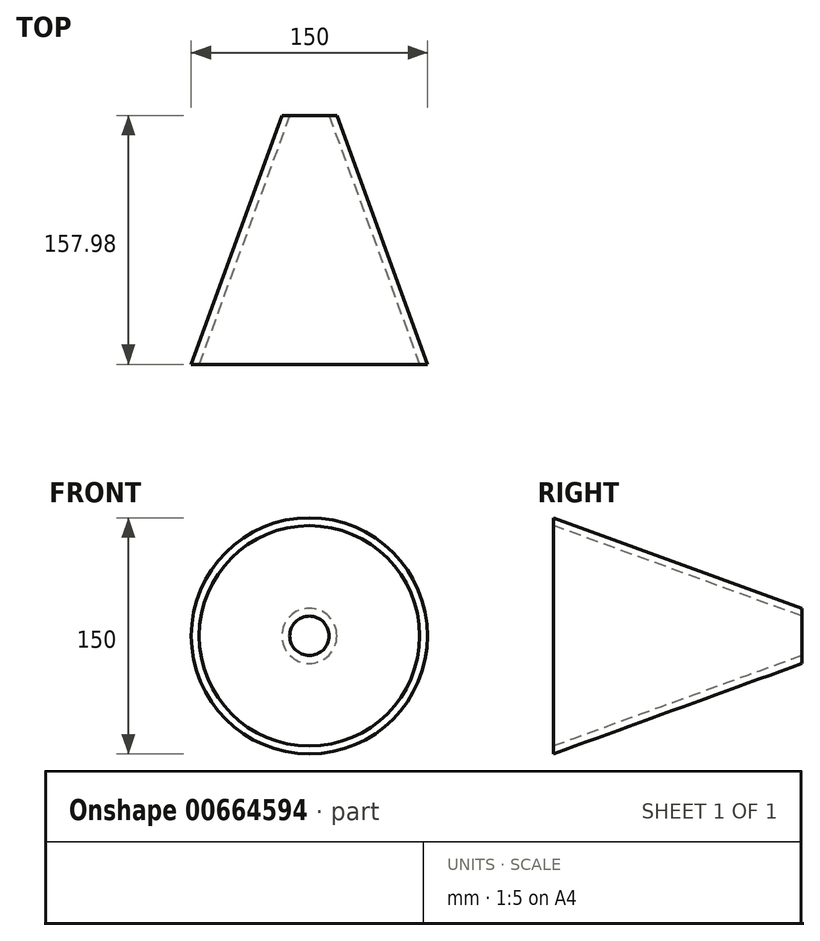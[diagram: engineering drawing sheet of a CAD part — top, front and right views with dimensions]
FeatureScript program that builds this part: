
annotation { "Feature Type Name" : "Feature", "Feature Type Description" : "" }
export const myFeature = defineFeature(function(context is Context, id is Id, definition is map)
    precondition{}
    {
        {
            var Q0;
            Q0=qCreatedBy(makeId("Right.planeOp"),FACE);
            var sketch = newSketch(context, id + "F0", { "sketchPlane" : qUnion([Q0])});
            skLineSegment(sketch, "E0", {"start": v(0, 75) * mm, "end": v(0, 70) * mm});
            skLineSegment(sketch, "E1", {"start": v(0, 70) * mm, "end": v(157.98, 12.5) * mm});
            skLineSegment(sketch, "E2", {"start": v(157.98, 12.5) * mm, "end": v(157.98, 17.5) * mm});
            skLineSegment(sketch, "E3", {"start": v(157.98, 17.5) * mm, "end": v(0, 75) * mm});
            skLineSegment(sketch, "E4", {"start": v(0, 0) * mm, "end": v(198.95, 0) * mm, "construction": true});
            skSolve(sketch);
        }
        {
            var Q0;
            Q0 = qSketchRegion(id + "F0", true);
            var Q1;
            Q1=sQuery(id+"F0.wireOp",EDGE,"E4");
            revolve(context, id + "F1", {"entities" : qUnion([Q0]), "axis" : qUnion([Q1]), "revolveType" : RevolveType.FULL});
        }
    });
